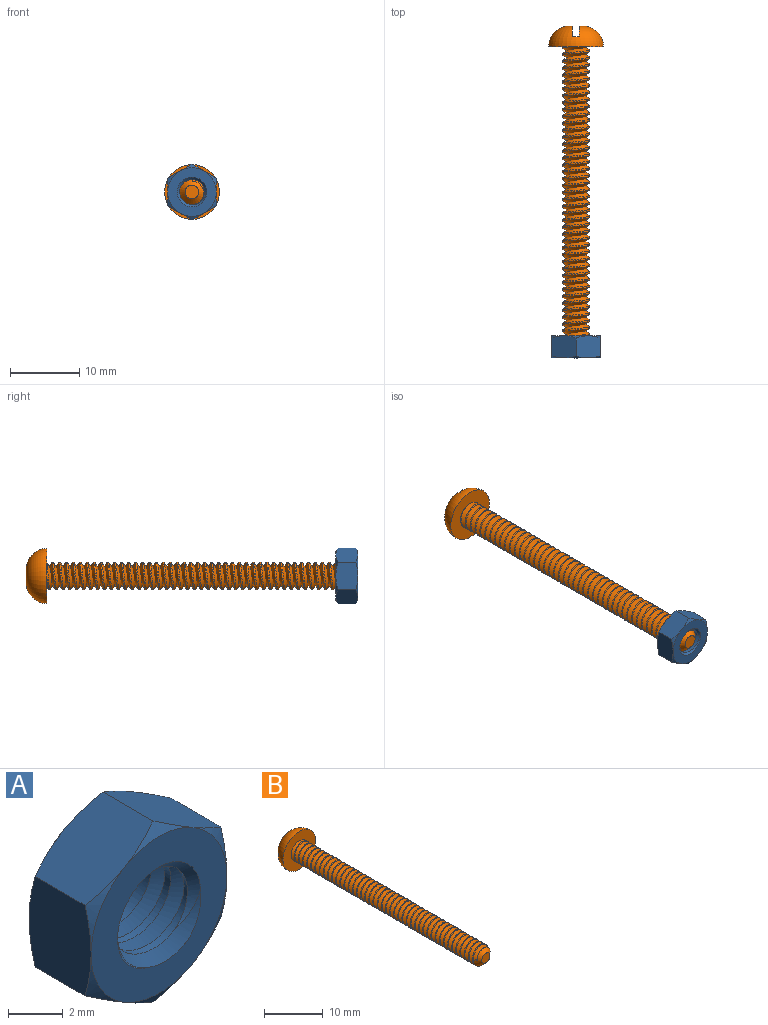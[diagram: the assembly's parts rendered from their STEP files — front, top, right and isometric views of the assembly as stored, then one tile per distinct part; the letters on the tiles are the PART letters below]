
ASSEMBLY  parts=2 mates=1
PART A: 26 faces, bbox 8.4x4x8.4 mm
  f0: cylinder r=1.8mm len=3.6mm, axis (0,1,0), area 9.7mm2, adj f1,f22,f23,f24,f25
  f1: cone r=2.14mm half-angle=45deg, axis (0,1,0), area 5.3mm2, adj f0,f3,f23,f24
  f2: plane 7.09x7.09mm, normal (0,-1,0), area 23.6mm2, adj f10,f11,f12,f13,f14,f15,f22,f24
  f3: plane 7x7mm, normal (0,1,0), area 24.1mm2, adj f1,f4,f5,f6,f7,f8,f9
  f4: cone r=5.74mm half-angle=60deg, axis (0,-1,0), area 1.2mm2, adj f3,f16,f21
  f5: cone r=5.74mm half-angle=60deg, axis (0,-1,0), area 1.2mm2, adj f3,f20,f21
  f6: cone r=5.74mm half-angle=60deg, axis (0,-1,0), area 1.2mm2, adj f3,f19,f20
  f7: cone r=5.74mm half-angle=60deg, axis (0,-1,0), area 1.2mm2, adj f3,f18,f19
  f8: cone r=5.74mm half-angle=60deg, axis (0,-1,0), area 1.2mm2, adj f3,f17,f18
  f9: cone r=5.74mm half-angle=60deg, axis (0,-1,0), area 1.2mm2, adj f3,f16,f17
  f10: cone r=5.74mm half-angle=60deg, axis (0,1,0), area 1.2mm2, adj f2,f16,f21
  f11: cone r=5.74mm half-angle=60deg, axis (0,1,0), area 1.2mm2, adj f2,f20,f21
  f12: cone r=5.74mm half-angle=60deg, axis (0,1,0), area 1.2mm2, adj f2,f19,f20
  f13: cone r=5.74mm half-angle=60deg, axis (0,1,0), area 1.2mm2, adj f2,f18,f19
  f14: cone r=5.74mm half-angle=60deg, axis (0,1,0), area 1.2mm2, adj f2,f17,f18
  f15: cone r=5.74mm half-angle=60deg, axis (0,1,0), area 1.2mm2, adj f2,f16,f17
  f16: plane 3.83x3.54mm, normal (-0.5,0,-0.87), area 12.1mm2, adj f4,f9,f10,f15,f17,f21
  f17: plane 4.38x3.54mm, normal (-1,0,0), area 12.1mm2, adj f8,f9,f14,f15,f16,f18
  f18: plane 3.83x3.54mm, normal (-0.5,0,0.87), area 12.1mm2, adj f7,f8,f13,f14,f17,f19
  f19: plane 3.83x3.54mm, normal (0.5,0,0.87), area 12.1mm2, adj f6,f7,f12,f13,f18,f20
  f20: plane 4.38x3.54mm, normal (1,0,0), area 12.1mm2, adj f5,f6,f11,f12,f19,f21
  f21: plane 3.83x3.54mm, normal (0.5,0,-0.87), area 12.1mm2, adj f4,f5,f10,f11,f16,f20
  f22: cone r=1.8mm half-angle=45deg, axis (0,-1,0), area 3.1mm2, adj f0,f2,f24,f25
  f23: plane 0.59x0.56mm, normal (0,0,1), area 0.2mm2, adj f0,f1,f24,f25
  f24: bspline ~5.53x4.79mm, area 26mm2, adj f0,f1,f2,f22,f23,f25
  f25: bspline ~5.53x4.79mm, area 23.6mm2, adj f0,f2,f22,f23,f24
PART B: 15 faces, bbox 7.9x48x7.9 mm
  f0: cylinder r=2mm len=44mm, axis (0,1,0), area 261.5mm2, adj f2,f3,f4,f5,f9
  f1: plane 2x2mm, normal (0,-1,0), area 3.1mm2, adj f2
  f2: cone r=1mm half-angle=45deg, axis (0,1,0), area 10.4mm2, adj f0,f1,f4,f5
  f3: bspline ~45.4x4.62mm, area 375.6mm2, adj f0,f4,f5,f10,f11
  f4: bspline ~45.4x4.62mm, area 371.6mm2, adj f0,f2,f3,f5,f10,f11
  f5: plane 0.69x0.53mm, normal (0,0,1), area 0.1mm2, adj f0,f2,f3,f4
  f6: plane 1.58x0.41mm, normal (0,1,0), area 0.5mm2, adj f7,f14
  f7: torus R=0.96mm, axis (0,-1,0), area 78.1mm2, adj f6,f8,f9,f12,f13,f14
  f8: plane 1.64x0.46mm, normal (0,1,0), area 0.5mm2, adj f7,f12
  f9: plane 7.91x7.91mm, normal (0,-1,0), area 36.6mm2, adj f0,f7,f11
  f10: plane 0.8x0.69mm, normal (0,0,-1), area 0.3mm2, adj f3,f4,f11
  f11: cylinder r=2mm len=4mm, axis (0,-1,0), area 6.5mm2, adj f3,f4,f9,f10
  f12: plane 7.13x1.58mm, normal (0,0,-1), area 8.8mm2, adj f7,f8,f13
  f13: plane 7.19x1.04mm, normal (0,1,0), area 7.4mm2, adj f7,f12,f14
  f14: plane 7.11x1.58mm, normal (0,0,1), area 8.7mm2, adj f6,f7,f13
PLACE A rot(axis=(1,0,0),180deg) t=(4.28,-25.13,-0.68)mm fixed
PLACE B rot(axis=(0,1,0),90deg) t=(4.28,19.87,-0.68)mm
MATE cylindrical A.f0 <-> B.f0  axis (0,-1,0) through (4.28,-25.13,-0.68)mm
